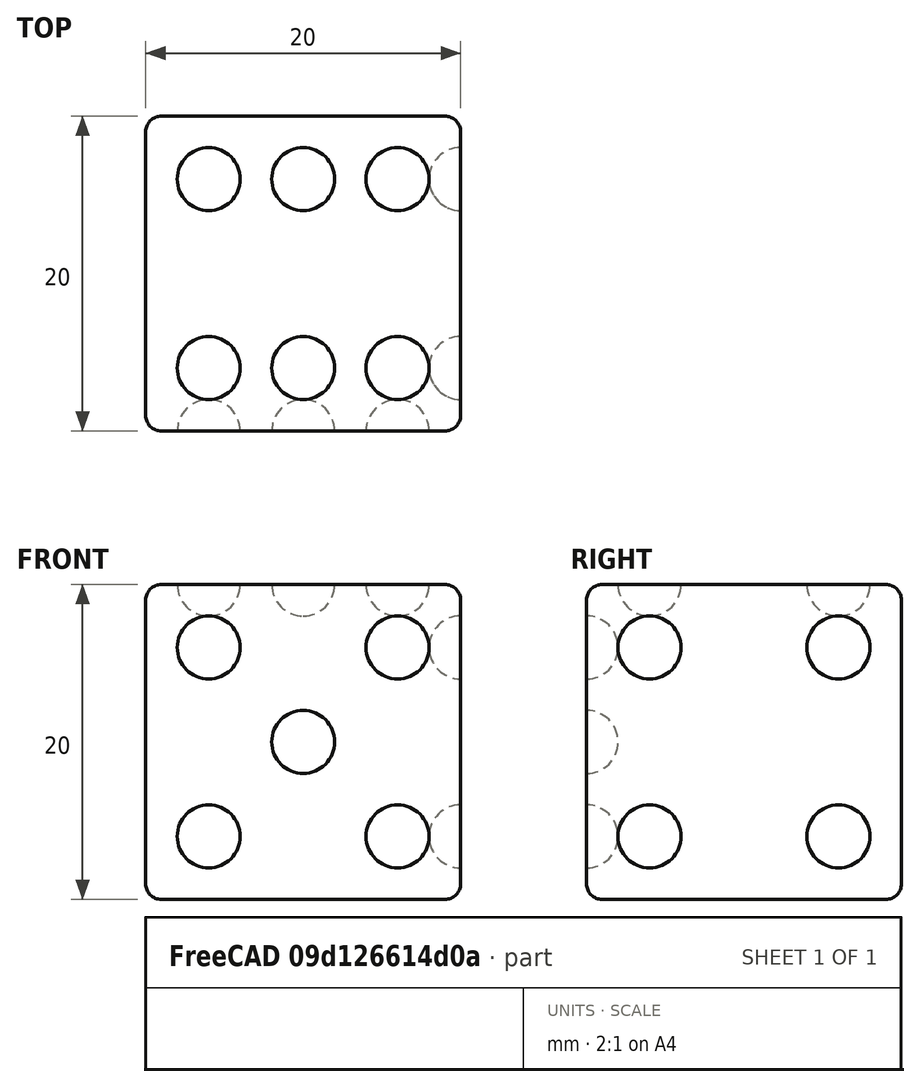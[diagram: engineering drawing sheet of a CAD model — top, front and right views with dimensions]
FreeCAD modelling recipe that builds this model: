
FCSTD DOCUMENT  (FreeCAD 1.0R39319 (Git))
Label: ojt1_t13r02_dado
License: All rights reserved
LicenseURL: https://en.wikipedia.org/wiki/All_rights_reserved
objects: Part::Sphere×15, Part::MultiFuse×6, Part::Cut×3, Part::Box×1, Part::Fillet×1
note: 26 computed .brp shape members not serialized (recipe doc carries the construction recipe); baked Part::Feature solids carry a one-line shape summary decoded from their .brp

FEATURE [Part::Box] Box  label="Cub"
  AttacherType = Attacher::AttachEngine3D
  Height = 20
  Length = 20
  Width = 20
FEATURE [Part::Fillet] Fillet
  Base = -> Box
  EdgeLinks = -> Box [Edge1,Edge2,Edge3,Edge4,Edge5,Edge6,Edge7,Edge8,Edge9,Edge10,Edge11,Edge12]
  Edges = 12 edges r=1: [Edge1,Edge2,Edge3,Edge4,Edge5,Edge6,Edge7,Edge8,Edge9,Edge10,Edge11,Edge12]
FEATURE [Part::Sphere] Sphere  label="Esfera"
  Angle1 = -90
  Angle2 = 90
  Angle3 = 360
  AttacherType = Attacher::AttachEngine3D
  Placement = pos=(4,4,20) rot=(0,0,1;0rad)
  Radius = 2
FEATURE [Part::Sphere] Sphere001  label="Esfera001"
  Angle1 = -90
  Angle2 = 90
  Angle3 = 360
  AttacherType = Attacher::AttachEngine3D
  Placement = pos=(10,4,20) rot=(0,0,1;0rad)
  Radius = 2
FEATURE [Part::Sphere] Sphere002  label="Esfera002"
  Angle1 = -90
  Angle2 = 90
  Angle3 = 360
  AttacherType = Attacher::AttachEngine3D
  Placement = pos=(16,4,20) rot=(0,0,1;0rad)
  Radius = 2
FEATURE [Part::MultiFuse] Fusion
  Refine = true
  Shapes = -> [Sphere,Sphere001,Sphere002]
FEATURE [Part::Sphere] Sphere003  label="Esfera003"
  Angle1 = -90
  Angle2 = 90
  Angle3 = 360
  AttacherType = Attacher::AttachEngine3D
  Placement = pos=(4,16,20) rot=(0,0,1;0rad)
  Radius = 2
FEATURE [Part::Sphere] Sphere004  label="Esfera004"
  Angle1 = -90
  Angle2 = 90
  Angle3 = 360
  AttacherType = Attacher::AttachEngine3D
  Placement = pos=(10,16,20) rot=(0,0,1;0rad)
  Radius = 2
FEATURE [Part::Sphere] Sphere005  label="Esfera005"
  Angle1 = -90
  Angle2 = 90
  Angle3 = 360
  AttacherType = Attacher::AttachEngine3D
  Placement = pos=(16,16,20) rot=(0,0,1;0rad)
  Radius = 2
FEATURE [Part::MultiFuse] Fusion001
  Refine = true
  Shapes = -> [Sphere003,Sphere004,Sphere005]
FEATURE [Part::MultiFuse] Fusion002  label="6"
  Refine = true
  Shapes = -> [Fusion,Fusion001]
FEATURE [Part::Sphere] Sphere006  label="Esfera006"
  Angle1 = -90
  Angle2 = 90
  Angle3 = 360
  AttacherType = Attacher::AttachEngine3D
  Placement = pos=(4,0,4) rot=(0,0,1;0rad)
  Radius = 2
FEATURE [Part::Sphere] Sphere007  label="Esfera007"
  Angle1 = -90
  Angle2 = 90
  Angle3 = 360
  AttacherType = Attacher::AttachEngine3D
  Placement = pos=(16,0,4) rot=(0,0,1;0rad)
  Radius = 2
FEATURE [Part::MultiFuse] Fusion003
  Refine = true
  Shapes = -> [Sphere006,Sphere007]
FEATURE [Part::Sphere] Sphere008  label="Esfera008"
  Angle1 = -90
  Angle2 = 90
  Angle3 = 360
  AttacherType = Attacher::AttachEngine3D
  Placement = pos=(4,0,16) rot=(0,0,1;0rad)
  Radius = 2
FEATURE [Part::Sphere] Sphere009  label="Esfera009"
  Angle1 = -90
  Angle2 = 90
  Angle3 = 360
  AttacherType = Attacher::AttachEngine3D
  Placement = pos=(16,0,16) rot=(0,0,1;0rad)
  Radius = 2
FEATURE [Part::Sphere] Sphere010  label="Esfera010"
  Angle1 = -90
  Angle2 = 90
  Angle3 = 360
  AttacherType = Attacher::AttachEngine3D
  Placement = pos=(10,0,10) rot=(0,0,1;0rad)
  Radius = 2
FEATURE [Part::MultiFuse] Fusion004  label="5"
  Refine = true
  Shapes = -> [Fusion003,Sphere008,Sphere009,Sphere010]
FEATURE [Part::Sphere] Sphere011  label="Esfera011"
  Angle1 = -90
  Angle2 = 90
  Angle3 = 360
  AttacherType = Attacher::AttachEngine3D
  Placement = pos=(20,4,4) rot=(0,0,1;0rad)
  Radius = 2
FEATURE [Part::Sphere] Sphere012  label="Esfera012"
  Angle1 = -90
  Angle2 = 90
  Angle3 = 360
  AttacherType = Attacher::AttachEngine3D
  Placement = pos=(20,16,4) rot=(0,0,1;0rad)
  Radius = 2
FEATURE [Part::Sphere] Sphere013  label="Esfera013"
  Angle1 = -90
  Angle2 = 90
  Angle3 = 360
  AttacherType = Attacher::AttachEngine3D
  Placement = pos=(20,4,16) rot=(0,0,1;0rad)
  Radius = 2
FEATURE [Part::Sphere] Sphere014  label="Esfera014"
  Angle1 = -90
  Angle2 = 90
  Angle3 = 360
  AttacherType = Attacher::AttachEngine3D
  Placement = pos=(20,16,16) rot=(0,0,1;0rad)
  Radius = 2
FEATURE [Part::MultiFuse] Fusion005  label="4"
  Refine = true
  Shapes = -> [Sphere011,Sphere012,Sphere013,Sphere014]
FEATURE [Part::Cut] Cut
  Base = -> Fillet
  Refine = true
  Tool = -> Fusion002
FEATURE [Part::Cut] Cut001
  Base = -> Cut
  Refine = true
  Tool = -> Fusion005
FEATURE [Part::Cut] Cut002  label="dau"
  Base = -> Cut001
  Refine = true
  Tool = -> Fusion004
